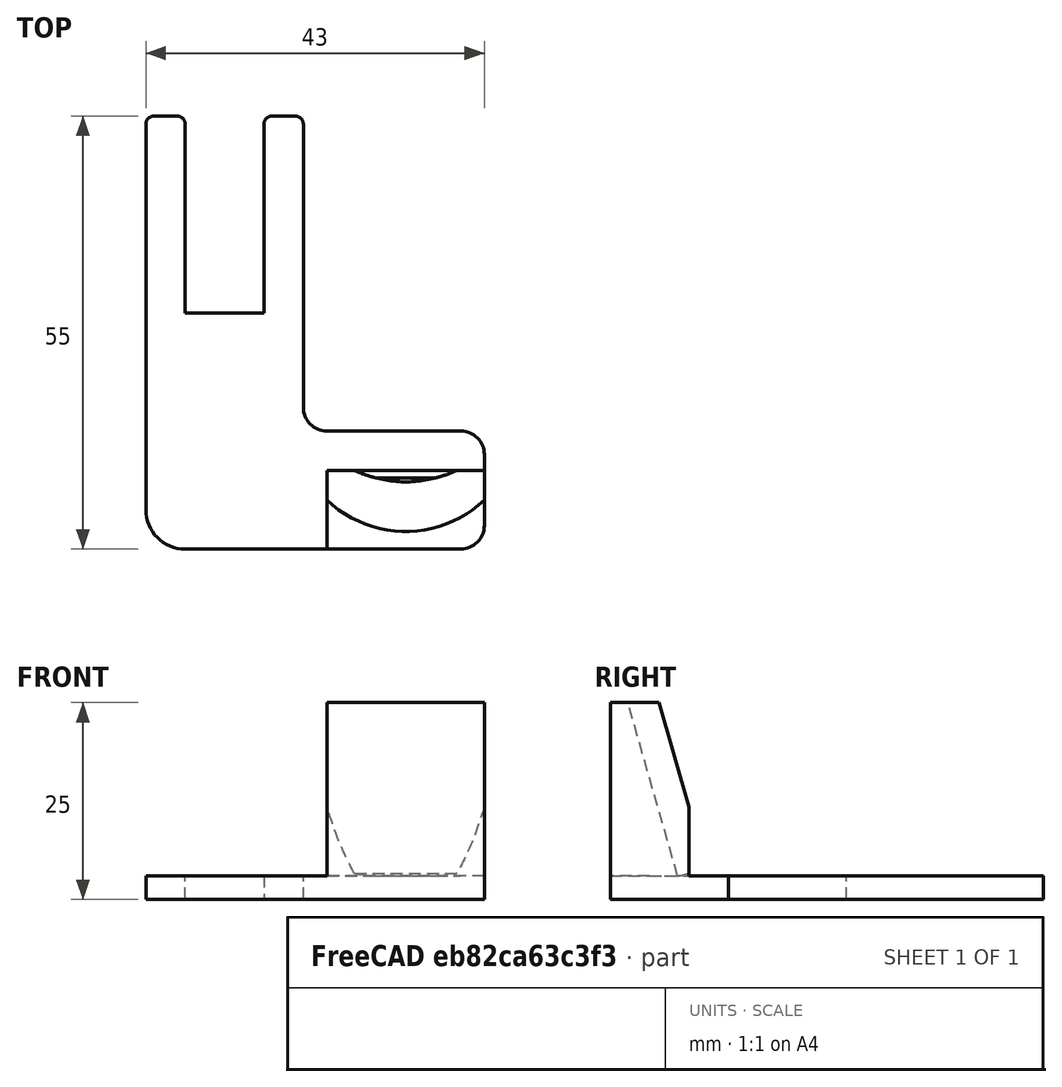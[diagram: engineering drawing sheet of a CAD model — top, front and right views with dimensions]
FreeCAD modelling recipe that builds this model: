
FCSTD DOCUMENT
Label: j-support_v2
objects: Part::Fillet×7, Part::Box×5, Part::Cut×3, Part::Fuse×3, Part::Cylinder×2
note: 20 computed .brp shape members not serialized (recipe doc carries the construction recipe); baked Part::Feature solids carry a one-line shape summary decoded from their .brp

FEATURE [Part::Box] Box  label="Box01"
  Height = 3
  Length = 20
  Width = 45
FEATURE [Part::Box] Box001  label="Box02"
  Height = 10
  Length = 10
  Placement = pos=(5,20,-3) rot=(0,0,1;0rad)
  Width = 30
FEATURE [Part::Cut] Cut  label="Patte"
  Base = -> Box
  Tool = -> Box001
FEATURE [Part::Box] Box002
  Height = 25
  Length = 20
  Placement = pos=(20,-10,0) rot=(0,0,1;0rad)
  Width = 10
FEATURE [Part::Cylinder] Cylinder
  Angle = 360
  Height = 27
  Placement = pos=(30,13,7) rot=(1,0,0;0.279252rad)
  Radius = 15
FEATURE [Part::Cut] Cut001  label="Prise"
  Base = -> Box002
  Placement = pos=(3,0,0) rot=(0,0,1;0rad)
  Tool = -> Cylinder
FEATURE [Part::Box] Box003  label="Extension plan"
  Height = 3
  Length = 43
  Placement = pos=(0,-10,0) rot=(0,0,1;0rad)
  Width = 15
FEATURE [Part::Fuse] Fusion
  Base = -> Cut
  Tool = -> Box003
FEATURE [Part::Box] Box004  label="Finition intérieure"
  Height = 3
  Length = 3
  Placement = pos=(20,5,0) rot=(0,0,1;0rad)
  Width = 3
FEATURE [Part::Fuse] Fusion001
  Base = -> Fusion
  Tool = -> Box004
FEATURE [Part::Fuse] Fusion002
  Base = -> Fusion001
  Tool = -> Cut001
FEATURE [Part::Fillet] Fillet
  Base = -> Fusion002
  Edges = 1 edges r=5: [Edge49]
FEATURE [Part::Fillet] Fillet001
  Base = -> Fillet
  Edges = 1 edges r=3: [Edge29]
FEATURE [Part::Fillet] Fillet002
  Base = -> Fillet001
  Edges = 1 edges r=3: [Edge47]
FEATURE [Part::Fillet] Fillet003
  Base = -> Fillet002
  Edges = 1 edges r=1: [Edge89]
FEATURE [Part::Fillet] Fillet004
  Base = -> Fillet003
  Edges = 1 edges r=1: [Edge25]
FEATURE [Part::Fillet] Fillet005
  Base = -> Fillet004
  Edges = 1 edges r=1: [Edge33]
FEATURE [Part::Fillet] Fillet006
  Base = -> Fillet005
  Edges = 1 edges r=1: [Edge38]
FEATURE [Part::Cylinder] Cylinder001
  Angle = 360
  Height = 10
  Placement = pos=(23,8,-1) rot=(0,0,1;0rad)
  Radius = 3
FEATURE [Part::Cut] Cut002
  Base = -> Fillet006
  Tool = -> Cylinder001
